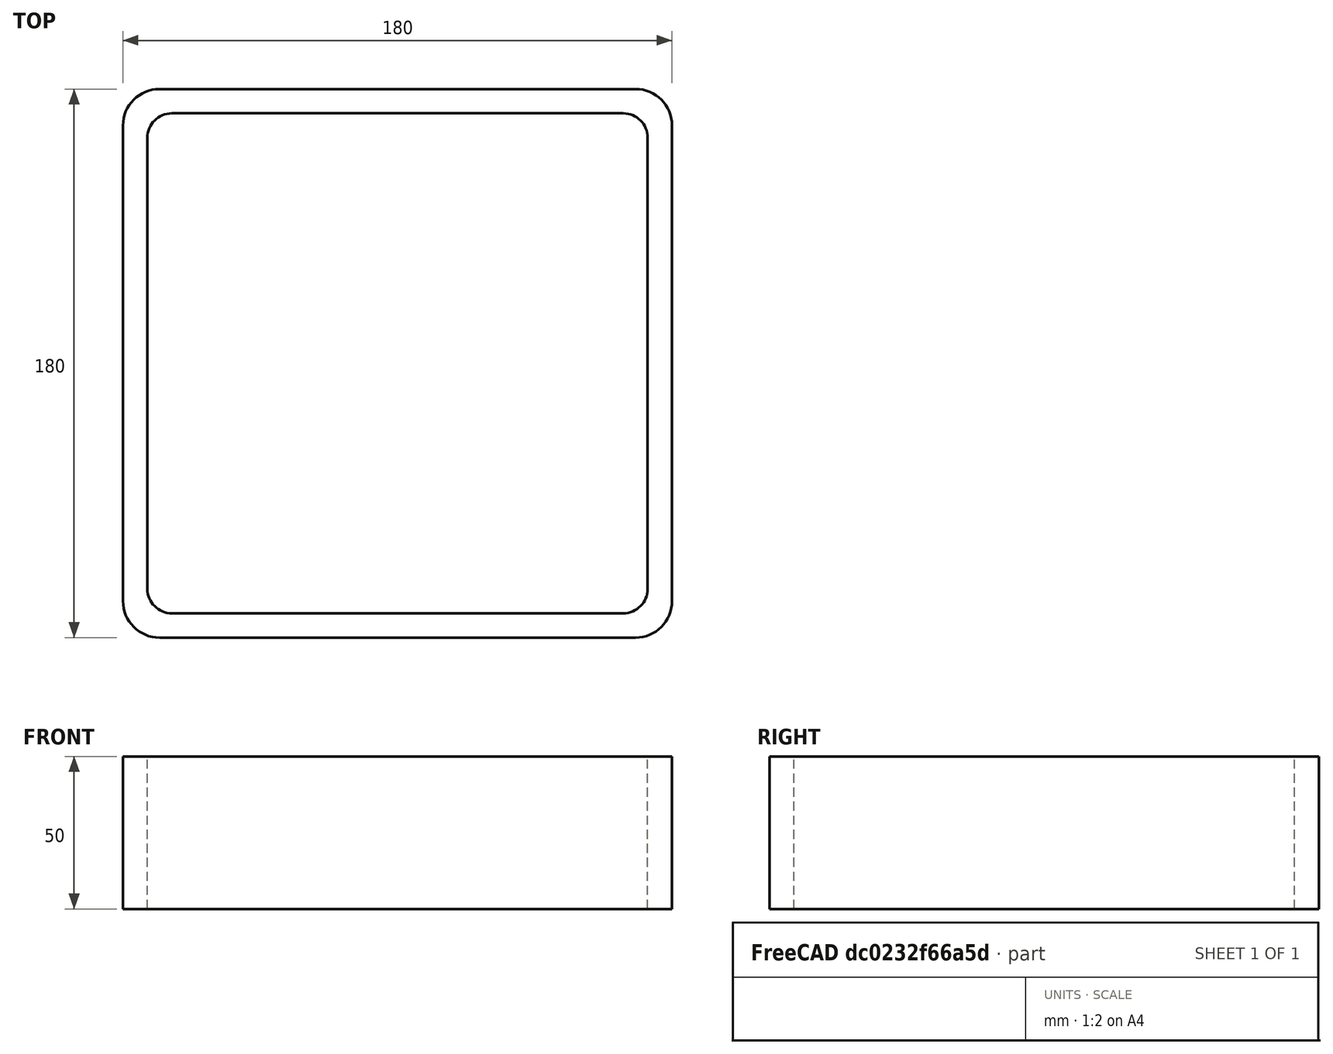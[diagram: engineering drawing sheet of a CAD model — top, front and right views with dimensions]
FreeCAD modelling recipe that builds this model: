
FCSTD DOCUMENT  (FreeCAD 0.15R4671 (Git))
Label: Square hollow section 180x180x8 EN10219 S235JRH
License: All rights reserved
LicenseURL: http://en.wikipedia.org/wiki/All_rights_reserved
objects: Sketcher::SketchObject×1, Part::Extrusion×1
note: 2 computed .brp shape members not serialized (recipe doc carries the construction recipe); baked Part::Feature solids carry a one-line shape summary decoded from their .brp

FEATURE [Sketcher::SketchObject] Sketch
  sketch-geometry (16):
    g0: LineSegment StartX=-74 StartY=82 StartZ=0 EndX=74 EndY=82 EndZ=0
    g1: LineSegment StartX=82 StartY=74 StartZ=0 EndX=82 EndY=-74 EndZ=0
    g2: LineSegment StartX=74 StartY=-82 StartZ=0 EndX=-74 EndY=-82 EndZ=0
    g3: LineSegment StartX=-82 StartY=-74 StartZ=0 EndX=-82 EndY=74 EndZ=0
    g4: LineSegment StartX=-78 StartY=90 StartZ=0 EndX=78 EndY=90 EndZ=0
    g5: LineSegment StartX=90 StartY=78 StartZ=0 EndX=90 EndY=-78 EndZ=0
    g6: LineSegment StartX=78 StartY=-90 StartZ=0 EndX=-78 EndY=-90 EndZ=0
    g7: LineSegment StartX=-90 StartY=-78 StartZ=0 EndX=-90 EndY=78 EndZ=0
    g8: ArcOfCircle CenterX=-74 CenterY=74 CenterZ=0 NormalX=0 NormalY=0 NormalZ=1 Radius=8 StartAngle=1.5708 EndAngle=3.14159
    g9: ArcOfCircle CenterX=74 CenterY=74 CenterZ=0 NormalX=0 NormalY=0 NormalZ=1 Radius=8 StartAngle=0 EndAngle=1.5708
    g10: ArcOfCircle CenterX=74 CenterY=-74 CenterZ=0 NormalX=0 NormalY=0 NormalZ=1 Radius=8 StartAngle=4.71239 EndAngle=6.28319
    g11: ArcOfCircle CenterX=-74 CenterY=-74 CenterZ=0 NormalX=0 NormalY=0 NormalZ=1 Radius=8 StartAngle=3.14159 EndAngle=4.71239
    g12: ArcOfCircle CenterX=78 CenterY=78 CenterZ=0 NormalX=0 NormalY=0 NormalZ=1 Radius=12 StartAngle=0 EndAngle=1.5708
    g13: ArcOfCircle CenterX=78 CenterY=-78 CenterZ=0 NormalX=0 NormalY=0 NormalZ=1 Radius=12 StartAngle=4.71239 EndAngle=6.28319
    g14: ArcOfCircle CenterX=-78 CenterY=-78 CenterZ=0 NormalX=0 NormalY=0 NormalZ=1 Radius=12 StartAngle=3.14159 EndAngle=4.71239
    g15: ArcOfCircle CenterX=-78 CenterY=78 CenterZ=0 NormalX=0 NormalY=0 NormalZ=1 Radius=12 StartAngle=1.5708 EndAngle=3.14159
  constraints (36):
    c: Horizontal(g2)
    c: Vertical(g3)
    c: Horizontal(g6)
    c: Vertical(g7)
    c: Tangent(g3,g8) = 1.5708
    c: Tangent(g0,g8) = 1.5708
    c: Tangent(g0,g9) = 1.5708
    c: Tangent(g1,g9) = 1.5708
    c: Tangent(g1,g10) = 1.5708
    c: Tangent(g2,g10) = 1.5708
    c: Tangent(g2,g11) = 1.5708
    c: Tangent(g3,g11) = 1.5708
    c: Tangent(g4,g12) = 1.5708
    c: Tangent(g5,g12) = 1.5708
    c: Tangent(g5,g13) = 1.5708
    c: Tangent(g6,g13) = 1.5708
    c: Tangent(g6,g14) = 1.5708
    c: Tangent(g7,g14) = 1.5708
    c: Tangent(g7,g15) = 1.5708
    c: Tangent(g4,g15) = 1.5708
    c: Equal(g9,g8)
    c: Equal(g9,g11)
    c: Equal(g9,g10)
    c: Equal(g12,g15)
    c: Equal(g12,g14)
    c: Equal(g12,g13)
    c: Symmetric(g4,g6,g-1)
    c: Symmetric(g7,g5,g-2)
    c: DistanceY(g4,g6) = -180
    c: DistanceX(g7,g5) = 180
    c: Symmetric(g3,g1,g-2)
    c: Symmetric(g0,g2,g-1)
    c: DistanceY(g0,g4) = 8
    c: DistanceX(g5,g1) = -8
    c: Radius(g9) = 8
    c: Radius(g12) = 12
FEATURE [Part::Extrusion] Extrude  label="Square hollow section 180x180x8 EN10219 S235JRH"
  Base = -> Sketch
  Dir = (0,0,50)
  Solid = true
